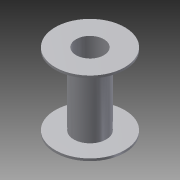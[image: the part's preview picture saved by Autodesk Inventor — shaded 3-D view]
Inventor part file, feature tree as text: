
AUTODESK INVENTOR PART (.ipt)
format: ipt  version: 2014 (Build 180170000, 170)  size: 95,232 bytes
history: native  units: mm
features: extrude x3, sketch x3
ambient origin geometry x8: Origin, YZ Plane, XZ Plane, XY Plane, X Axis, Y Axis, Z Axis, Center Point
bodies: Solid1 (feature_tree)
feature tree (6):
  extrude  "Extrusion1"  Depth=15.0mm
  extrude  "Extrusion2"  Depth=0.5mm
  extrude  "Extrusion3"  Depth=0.5mm TaperAngle=0.0deg
  sketch  "Sketch1"  dims[d0=6.0mm d1=15.0mm]
  sketch  "Sketch2"  dims[d2=0.5mm d3=0.0mm d4=7.0mm]
  sketch  "Sketch3"  dims[d5=15.0mm d6=0.0mm d7=0.5mm d8=0.0mm]
